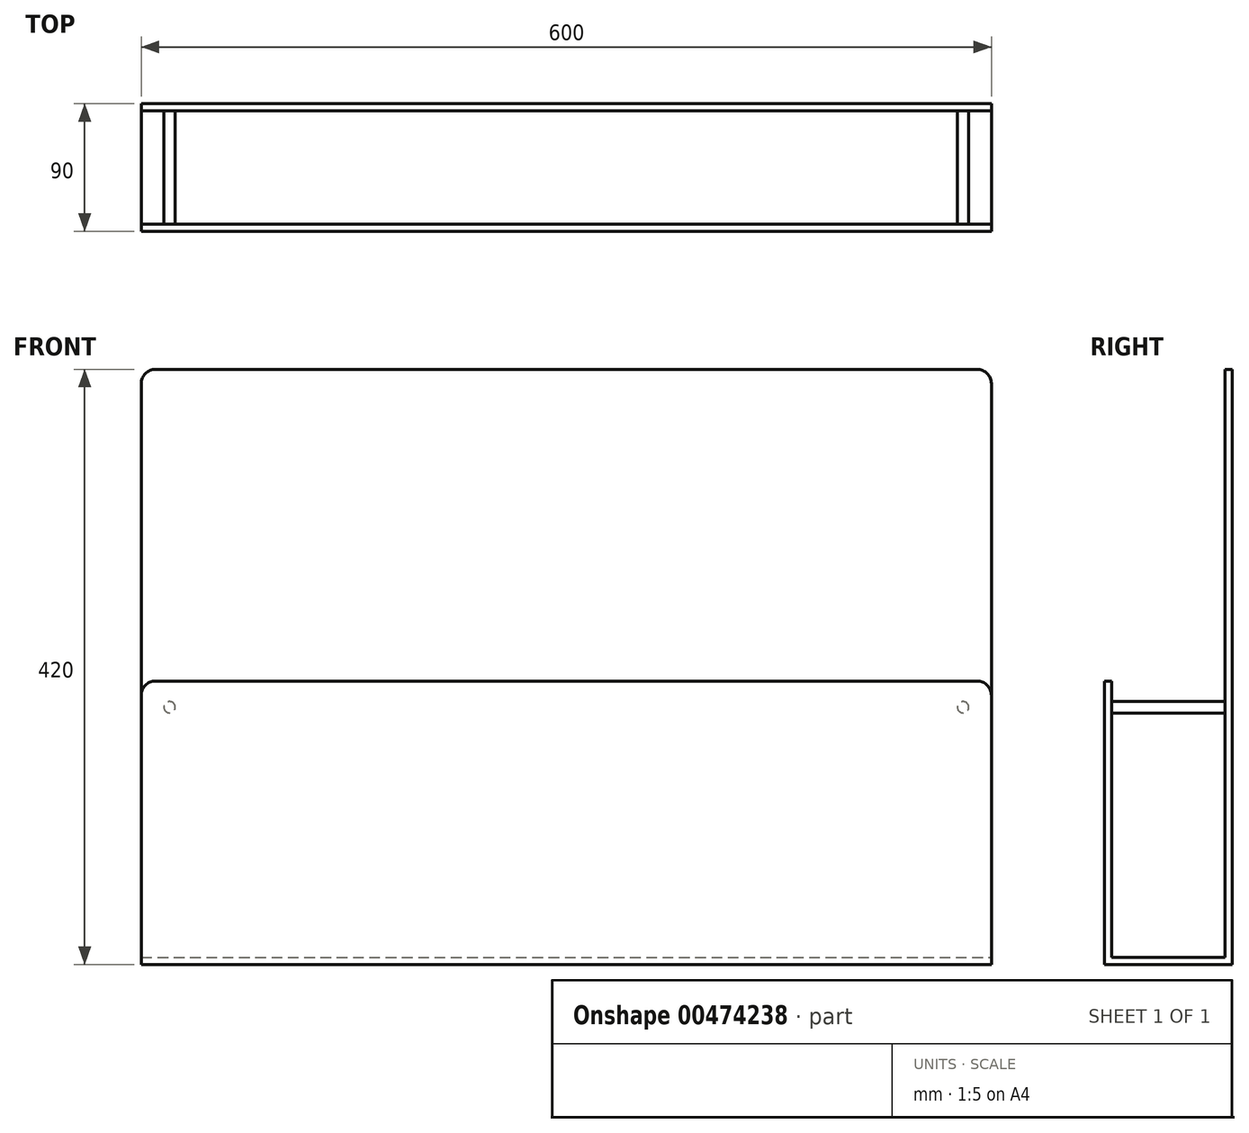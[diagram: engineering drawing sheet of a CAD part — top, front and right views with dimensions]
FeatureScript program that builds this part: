
annotation { "Feature Type Name" : "Feature", "Feature Type Description" : "" }
export const myFeature = defineFeature(function(context is Context, id is Id, definition is map)
    precondition{}
    {
        {
            var Q0;
            Q0=qCreatedBy(makeId("Front.planeOp"),FACE);
            var sketch = newSketch(context, id + "F0", { "sketchPlane" : qUnion([Q0])});
            skLineSegment(sketch, "E0.bottom", {"start": v(-553.45, 400.27) * mm, "end": v(26.55, 400.27) * mm});
            skLineSegment(sketch, "E0.top", {"start": v(-563.45, -19.73) * mm, "end": v(36.55, -19.73) * mm});
            skLineSegment(sketch, "E0.left", {"start": v(-563.45, 390.27) * mm, "end": v(-563.45, -19.73) * mm});
            skLineSegment(sketch, "E0.right", {"start": v(36.55, 390.27) * mm, "end": v(36.55, -19.73) * mm});
            skPoint(sketch, "E1.visualSharp", {"position": v(-563.45, 400.27) * mm});
            skArc(sketch, "E1.filletArc", {"start": v(-553.45, 400.27) * mm, "mid": v(-560.53, 397.35) * mm, "end": v(-563.45, 390.27) * mm});
            skPoint(sketch, "E2.visualSharp", {"position": v(36.55, 400.27) * mm});
            skArc(sketch, "E2.filletArc", {"start": v(36.55, 390.27) * mm, "mid": v(33.62, 397.35) * mm, "end": v(26.55, 400.27) * mm});
            skSolve(sketch);
        }
        {
            var Q0;
            Q0=makeQuery(id+"F0.imprint","IMPRINT",FACE,{"disambiguationData":[TD([[makeQuery(id+"F0.imprint","IMPRINT",EDGE,{"derivedFrom":sQuery(id+"F0.wireOp",EDGE,"E0.bottom")}),-1.0]])]});
            var Q1;
            Q1=makeQuery(id+"F0.imprint","IMPRINT",FACE,{"disambiguationData":[TD([[makeQuery(id+"F0.imprint","IMPRINT",EDGE,{"derivedFrom":sQuery(id+"F0.wireOp",EDGE,"E0.top")}),-1.0]])]});
            var Q2;
            Q2=makeQuery(id+"F0.imprint","IMPRINT",FACE,{"disambiguationData":[TD([[makeQuery(id+"F0.imprint","IMPRINT",EDGE,{"derivedFrom":sQuery(id+"F0.wireOp",EDGE,"vecummdt-QAZJ-KlPl-L39E-hd9chvPdwRKy.bottom")}),-1.0]])]});
            extrude(context, id + "F1", {"entities" : qUnion([Q0, Q1, Q2]), "depth" : 5 * mm});
        }
        {
            var Q0;
            Q0=makeQuery(id+"F1.opExtrude","CAP_FACE",FACE,{"disambiguationData":[OSD([sQuery(id+"F0.wireOp",EDGE,"E0.bottom"),sQuery(id+"F0.wireOp",EDGE,"E0.left"),sQuery(id+"F0.wireOp",EDGE,"E0.right"),sQuery(id+"F0.wireOp",EDGE,"E0.top"),sQuery(id+"F0.wireOp",EDGE,"E1.filletArc"),sQuery(id+"F0.wireOp",EDGE,"E2.filletArc")])],"isStart":false});
            var sketch = newSketch(context, id + "F2", { "sketchPlane" : qUnion([Q0])});
            skLineSegment(sketch, "E3.bottom", {"start": v(-563.45, -19.73) * mm, "end": v(36.55, -19.73) * mm});
            skLineSegment(sketch, "E3.top", {"start": v(-563.45, -14.73) * mm, "end": v(36.55, -14.73) * mm});
            skLineSegment(sketch, "E3.left", {"start": v(-563.45, -19.73) * mm, "end": v(-563.45, -14.73) * mm});
            skLineSegment(sketch, "E3.right", {"start": v(36.55, -19.73) * mm, "end": v(36.55, -14.73) * mm});
            skSolve(sketch);
        }
        {
            var Q0;
            Q0 = qSketchRegion(id + "F2", true);
            extrude(context, id + "F3", {"entities" : qUnion([Q0]), "operationType" : NewBodyOperationType.ADD, "depth" : 80 * mm});
        }
        {
            var Q0;
            Q0=makeQuery(id+"F3.opExtrude","CAP_FACE",FACE,{"disambiguationData":[OSD([sQuery(id+"F2.wireOp",EDGE,"E3.bottom"),sQuery(id+"F2.wireOp",EDGE,"E3.top"),sQuery(id+"F2.wireOp",EDGE,"E3.left"),sQuery(id+"F2.wireOp",EDGE,"E3.right")])],"isStart":false});
            var sketch = newSketch(context, id + "F4", { "sketchPlane" : qUnion([Q0])});
            skLineSegment(sketch, "E4.bottom", {"start": v(-563.45, -19.73) * mm, "end": v(36.55, -19.73) * mm});
            skLineSegment(sketch, "E4.top", {"start": v(-563.45, 180.27) * mm, "end": v(36.55, 180.27) * mm});
            skLineSegment(sketch, "E4.left", {"start": v(-563.45, -19.73) * mm, "end": v(-563.45, 180.27) * mm});
            skLineSegment(sketch, "E4.right", {"start": v(36.55, -19.73) * mm, "end": v(36.55, 180.27) * mm});
            skSolve(sketch);
        }
        {
            var Q0;
            {var subQ0=sQuery(id+"F4.wireOp",EDGE,"E4.bottom");Q0=makeQuery(id+"F4.imprint","IMPRINT",FACE,{"disambiguationData":[TD([[makeQuery(id+"F4.imprint","IMPRINT",EDGE,{"derivedFrom":subQ0}),1.0]])]});}
            var Q1;
            {var subQ0=sQuery(id+"F4.wireOp",EDGE,"E4.top");Q1=makeQuery(id+"F4.imprint","IMPRINT",FACE,{"disambiguationData":[TD([[makeQuery(id+"F4.imprint","IMPRINT",EDGE,{"derivedFrom":subQ0}),-1.0]])]});}
            extrude(context, id + "F5", {"entities" : qUnion([Q0, Q1]), "operationType" : NewBodyOperationType.ADD, "depth" : 5 * mm});
        }
        {
            var Q0;
            Q0=makeQuery(id+"F5.opExtrude","SWEPT_EDGE",EDGE,{"disambiguationData":[OSD([sQuery(id+"F4.wireOp",EDGE,"E4.top"),sQuery(id+"F4.wireOp",EDGE,"E4.left")])]});
            var Q1;
            Q1=makeQuery(id+"F5.opExtrude","SWEPT_EDGE",EDGE,{"disambiguationData":[OSD([sQuery(id+"F4.wireOp",EDGE,"E4.top"),sQuery(id+"F4.wireOp",EDGE,"E4.right")])]});
            fillet(context, id + "F6", {"entities" : qUnion([Q0, Q1]), "radius" : 10 * mm, "tangentPropagation" : true, "allowEdgeOverflow" : false});
        }
        {
            var Q0;
            Q0=makeQuery(id+"F5.opExtrude","CAP_FACE",FACE,{"disambiguationData":[OSD([sQuery(id+"F4.wireOp",EDGE,"E4.bottom"),sQuery(id+"F4.wireOp",EDGE,"E4.top"),sQuery(id+"F4.wireOp",EDGE,"E4.left"),sQuery(id+"F4.wireOp",EDGE,"E4.right")])],"isStart":false});
            var sketch = newSketch(context, id + "F7", { "sketchPlane" : qUnion([Q0])});
            skCircle(sketch, "E5", {"center": v(-543.45, 161.77) * mm, "radius": 4 * mm});
            skCircle(sketch, "E6", {"center": v(16.55, 161.77) * mm, "radius": 4 * mm});
            skSolve(sketch);
        }
        {
            var Q0;
            Q0=makeQuery(id+"F7.imprint","IMPRINT",FACE,{"disambiguationData":[TD([[makeQuery(id+"F7.imprint","IMPRINT",EDGE,{"derivedFrom":sQuery(id+"F7.wireOp",EDGE,"E5")}),1.0]])]});
            var Q1;
            Q1=makeQuery(id+"F7.imprint","IMPRINT",FACE,{"disambiguationData":[TD([[makeQuery(id+"F7.imprint","IMPRINT",EDGE,{"derivedFrom":sQuery(id+"F7.wireOp",EDGE,"E6")}),1.0]])]});
            extrude(context, id + "F8", {"entities" : qUnion([Q0, Q1]), "operationType" : NewBodyOperationType.ADD, "oppositeDirection" : true, "depth" : 85 * mm});
        }
    });
